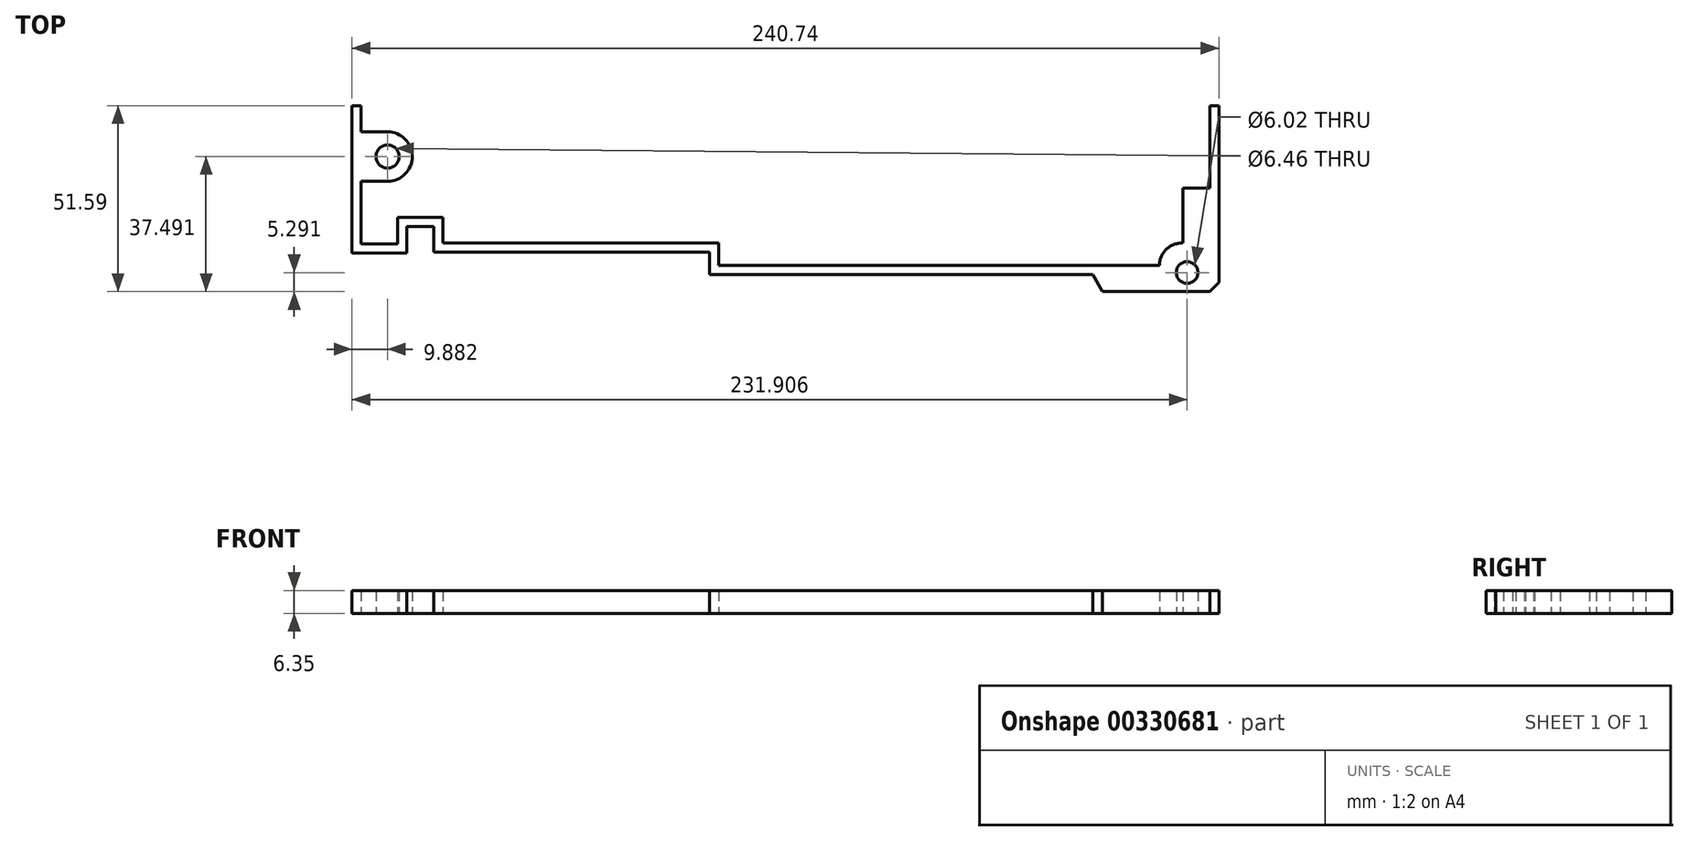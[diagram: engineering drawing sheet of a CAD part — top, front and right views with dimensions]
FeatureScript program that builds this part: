
annotation { "Feature Type Name" : "Feature", "Feature Type Description" : "" }
export const myFeature = defineFeature(function(context is Context, id is Id, definition is map)
    precondition{}
    {
        {
            var Q0;
            Q0=qCreatedBy(makeId("Top.planeOp"),FACE);
            var sketch = newSketch(context, id + "F0", { "sketchPlane" : qUnion([Q0])});
            skLineSegment(sketch, "E0.bottom", {"start": v(138.9, -131.49) * mm, "end": v(-128.52, -131.49) * mm});
            skLineSegment(sketch, "E0.top", {"start": v(138.9, 108.07) * mm, "end": v(-128.52, 108.07) * mm});
            skLineSegment(sketch, "E0.left", {"start": v(138.9, -131.49) * mm, "end": v(138.9, 108.07) * mm});
            skLineSegment(sketch, "E0.right", {"start": v(-128.52, -131.49) * mm, "end": v(-128.52, 108.07) * mm});
            skCircle(sketch, "E1", {"center": v(-91.95, 93.97) * mm, "radius": 3.26 * mm});
            skCircle(sketch, "E2", {"center": v(130.06, 61.76) * mm, "radius": 3.11 * mm});
            skLineSegment(sketch, "E3", {"start": v(-91.95, 93.97) * mm, "end": v(-101.34, 93.97) * mm, "construction": true});
            skLineSegment(sketch, "E4", {"start": v(-101.34, 93.6) * mm, "end": v(-101.34, 68.03) * mm});
            skSolve(sketch);
        }
        {
            var Q0;
            Q0=makeQuery(id+"F0.imprint","IMPRINT",FACE,{"disambiguationData":[TD([[makeQuery(id+"F0.imprint","IMPRINT",EDGE,{"derivedFrom":sQuery(id+"F0.wireOp",EDGE,"E0.bottom")}),-1.0]])]});
            var sketch = newSketch(context, id + "F1", { "sketchPlane" : qUnion([Q0])});
            skCircle(sketch, "E5", {"center": v(-91.95, 93.97) * mm, "radius": 3.23 * mm});
            skCircle(sketch, "E6", {"center": v(130.08, 61.77) * mm, "radius": 3.01 * mm});
            skLineSegment(sketch, "E7", {"start": v(-91.95, 93.97) * mm, "end": v(-91.95, 100.83) * mm, "construction": true});
            skLineSegment(sketch, "E8", {"start": v(-91.95, 93.97) * mm, "end": v(-91.95, 87.1) * mm, "construction": true});
            skArc(sketch, "E9", {"start": v(-91.95, 100.83) * mm, "mid": v(-85.09, 93.97) * mm, "end": v(-91.95, 87.1) * mm});
            skLineSegment(sketch, "E10", {"start": v(-91.95, 87.1) * mm, "end": v(-99.3, 87.1) * mm});
            skLineSegment(sketch, "E11", {"start": v(-99.3, 87.1) * mm, "end": v(-99.3, 69.74) * mm});
            skLineSegment(sketch, "E12", {"start": v(-99.3, 69.74) * mm, "end": v(-89.13, 69.74) * mm});
            skLineSegment(sketch, "E13", {"start": v(-89.13, 69.74) * mm, "end": v(-89.13, 77.02) * mm});
            skLineSegment(sketch, "E14", {"start": v(-89.13, 77.02) * mm, "end": v(-76.61, 77.02) * mm});
            skLineSegment(sketch, "E15", {"start": v(-76.61, 77.02) * mm, "end": v(-76.61, 69.96) * mm});
            skLineSegment(sketch, "E16", {"start": v(-76.61, 69.96) * mm, "end": v(0, 69.96) * mm});
            skLineSegment(sketch, "E17", {"start": v(0, 69.96) * mm, "end": v(0, 63.8) * mm});
            skLineSegment(sketch, "E18", {"start": v(0, 63.8) * mm, "end": v(104.6, 63.8) * mm});
            skLineSegment(sketch, "E19", {"start": v(-91.95, 100.83) * mm, "end": v(-99.3, 100.83) * mm});
            skLineSegment(sketch, "E20", {"start": v(-99.3, 100.83) * mm, "end": v(-99.3, 108.07) * mm});
            skLineSegment(sketch, "E21", {"start": v(-99.3, 108.07) * mm, "end": v(-101.83, 108.07) * mm});
            skLineSegment(sketch, "E22", {"start": v(-101.83, 108.07) * mm, "end": v(-101.83, 67.2) * mm});
            skLineSegment(sketch, "E23", {"start": v(-101.83, 67.2) * mm, "end": v(-86.6, 67.2) * mm});
            skLineSegment(sketch, "E24", {"start": v(-86.6, 67.2) * mm, "end": v(-86.6, 74.48) * mm});
            skLineSegment(sketch, "E25", {"start": v(-86.6, 74.48) * mm, "end": v(-79.15, 74.48) * mm});
            skLineSegment(sketch, "E26", {"start": v(-79.15, 74.48) * mm, "end": v(-79.15, 67.42) * mm});
            skLineSegment(sketch, "E27", {"start": v(-79.15, 67.42) * mm, "end": v(-2.54, 67.42) * mm});
            skLineSegment(sketch, "E28", {"start": v(-2.54, 67.42) * mm, "end": v(-2.54, 61.25) * mm});
            skLineSegment(sketch, "E29", {"start": v(-2.54, 61.25) * mm, "end": v(103.91, 61.25) * mm});
            skLineSegment(sketch, "E30", {"start": v(104.6, 63.8) * mm, "end": v(122.38, 63.8) * mm});
            skLineSegment(sketch, "E31", {"start": v(128.94, 69.97) * mm, "end": v(128.94, 85.21) * mm});
            skLineSegment(sketch, "E32", {"start": v(128.94, 85.21) * mm, "end": v(136.37, 85.21) * mm});
            skLineSegment(sketch, "E33", {"start": v(136.37, 85.21) * mm, "end": v(136.37, 108.07) * mm});
            skLineSegment(sketch, "E34", {"start": v(136.37, 108.07) * mm, "end": v(138.9, 108.07) * mm});
            skLineSegment(sketch, "E35", {"start": v(138.9, 108.07) * mm, "end": v(138.9, 59.1) * mm});
            skLineSegment(sketch, "E36", {"start": v(138.9, 59.1) * mm, "end": v(136.37, 56.48) * mm});
            skLineSegment(sketch, "E37", {"start": v(136.37, 56.48) * mm, "end": v(106.53, 56.48) * mm});
            skLineSegment(sketch, "E38", {"start": v(106.53, 56.48) * mm, "end": v(103.91, 61.25) * mm});
            skArc(sketch, "E39", {"start": v(128.94, 69.97) * mm, "mid": v(124.35, 68.27) * mm, "end": v(122.38, 63.8) * mm});
            skLineSegment(sketch, "E40", {"start": v(-89.13, 71.56) * mm, "end": v(-86.6, 71.56) * mm, "construction": true});
            skLineSegment(sketch, "E41", {"start": v(-101.83, 106.03) * mm, "end": v(-99.3, 106.03) * mm, "construction": true});
            skLineSegment(sketch, "E42", {"start": v(-101.83, 85.98) * mm, "end": v(-99.3, 85.98) * mm, "construction": true});
            skLineSegment(sketch, "E43", {"start": v(-97.14, 67.2) * mm, "end": v(-97.14, 69.74) * mm, "construction": true});
            skLineSegment(sketch, "E44", {"start": v(-79.15, 70.95) * mm, "end": v(-76.61, 70.95) * mm, "construction": true});
            skLineSegment(sketch, "E45", {"start": v(-83.5, 74.48) * mm, "end": v(-83.5, 77.02) * mm});
            skLineSegment(sketch, "E46", {"start": v(-9.56, 67.42) * mm, "end": v(-9.56, 69.96) * mm, "construction": true});
            skLineSegment(sketch, "E47", {"start": v(-2.54, 64.76) * mm, "end": v(0, 64.76) * mm, "construction": true});
            skLineSegment(sketch, "E48", {"start": v(5.43, 61.25) * mm, "end": v(5.43, 63.8) * mm, "construction": true});
            skLineSegment(sketch, "E49", {"start": v(136.37, 99.69) * mm, "end": v(138.9, 99.69) * mm, "construction": true});
            skSolve(sketch);
        }
        {
            var Q0;
            Q0 = qSketchRegion(id + "F1", true);
            extrude(context, id + "F2", {"entities" : qUnion([Q0]), "depth" : 6.35 * mm});
        }
    });
